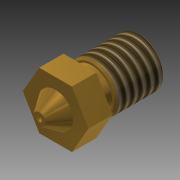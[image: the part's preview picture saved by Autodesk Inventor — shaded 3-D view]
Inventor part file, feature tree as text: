
AUTODESK INVENTOR PART (.ipt)
format: ipt  version: 2015 (Build 190159000, 159)  size: 144,384 bytes
history: native  units: mm
features: sketch x4, chamfer x2, hole x2, other x1, revolve x1, thread x1, extrude x1
ambient origin geometry x8: Origin, YZ Plane, XZ Plane, XY Plane, X Axis, Y Axis, Z Axis, Center Point
bodies: Body1 (feature_tree)
feature tree (12):
  other  "Твердое тело1"
  revolve  "Вращение1"
  chamfer  "Фаска1"  Distance=15.0mm
  thread  "Резьба1"
  sketch  "Эскиз2"
  sketch  "Эскиз3"
  hole  "Отверстие2"  [1 undecoded]
  chamfer  "Фаска2"  Distance=10.5mm
  hole  "Отверстие3"  [1 undecoded]
  extrude  "Выдавливание1"  Depth=6.0mm
  sketch  "Эскиз1"
  sketch  "Эскиз4"
note: 2 required parameter values undecoded (feature->parameter linkage not recoverable at this tier; creation-order binding heuristic only, values carry confidence <= 0.55)
